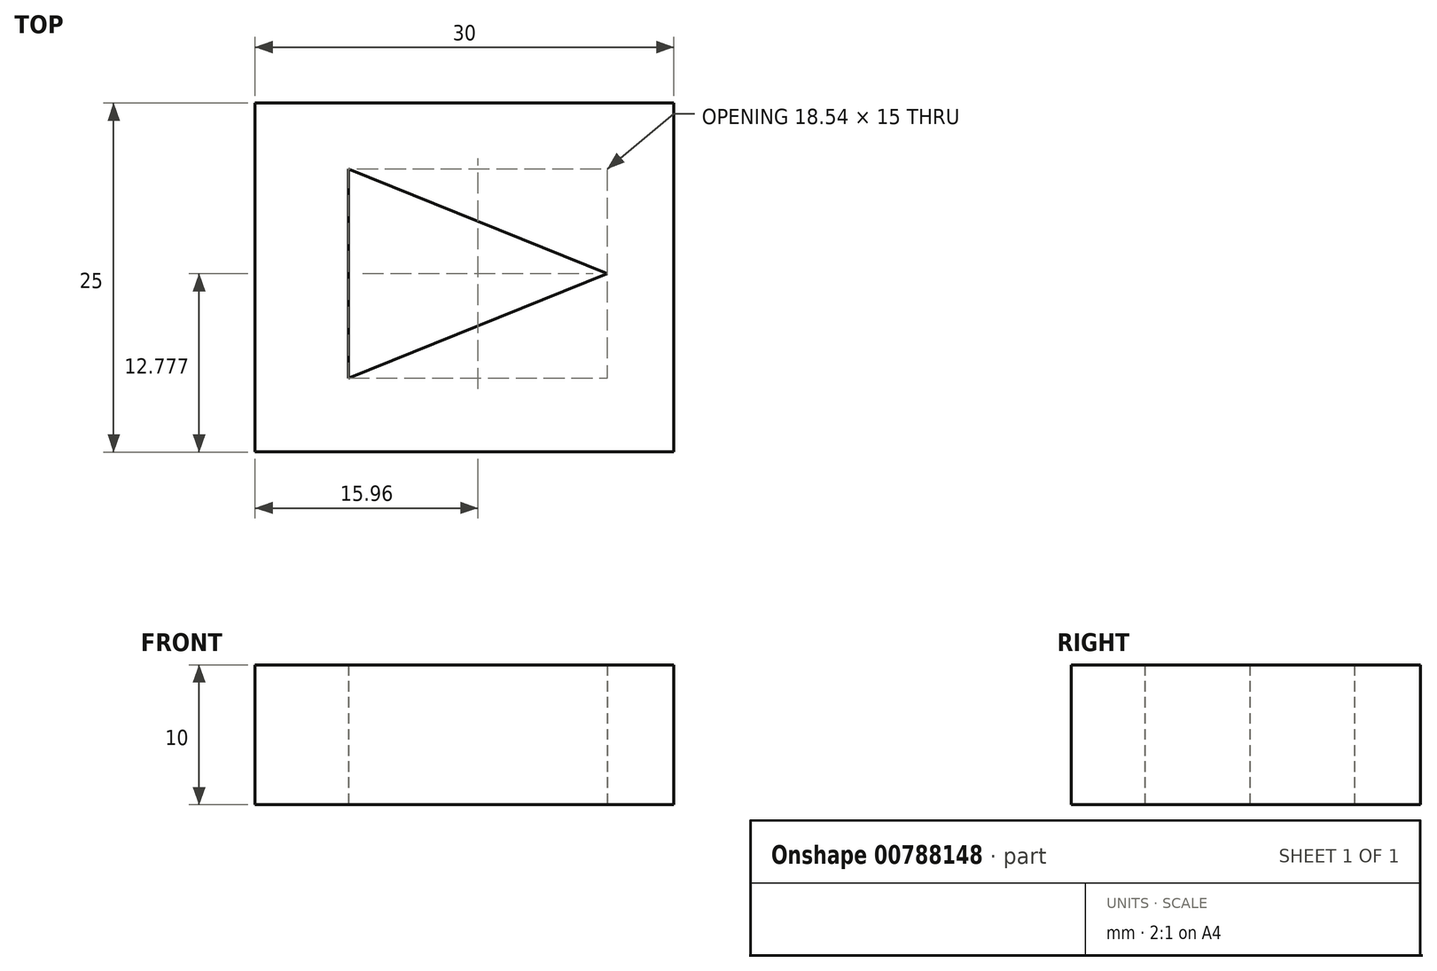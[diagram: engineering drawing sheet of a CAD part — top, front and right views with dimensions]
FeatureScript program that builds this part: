
annotation { "Feature Type Name" : "Feature", "Feature Type Description" : "" }
export const myFeature = defineFeature(function(context is Context, id is Id, definition is map)
    precondition{}
    {
        {
            var Q0;
            Q0=qCreatedBy(makeId("Top.planeOp"),FACE);
            var sketch = newSketch(context, id + "F0", { "sketchPlane" : qUnion([Q0])});
            skLineSegment(sketch, "E0.bottom", {"start": v(-26.14, 10.8) * mm, "end": v(3.86, 10.8) * mm});
            skLineSegment(sketch, "E0.top", {"start": v(-26.14, -14.2) * mm, "end": v(3.86, -14.2) * mm});
            skLineSegment(sketch, "E0.left", {"start": v(-26.14, 10.8) * mm, "end": v(-26.14, -14.2) * mm});
            skLineSegment(sketch, "E0.right", {"start": v(3.86, 10.8) * mm, "end": v(3.86, -14.2) * mm});
            skLineSegment(sketch, "E1", {"start": v(-19.45, 6.07) * mm, "end": v(-19.45, -8.93) * mm});
            skLineSegment(sketch, "E2", {"start": v(-19.45, -8.93) * mm, "end": v(-0.9, -1.43) * mm});
            skLineSegment(sketch, "E3", {"start": v(-0.9, -1.43) * mm, "end": v(-19.45, 6.07) * mm});
            skSolve(sketch);
        }
        {
            var Q0;
            Q0=makeQuery(id+"F0.imprint","IMPRINT",FACE,{"disambiguationData":[TD([[makeQuery(id+"F0.imprint","IMPRINT",EDGE,{"derivedFrom":sQuery(id+"F0.wireOp",EDGE,"E0.bottom")}),-1.0]])]});
            extrude(context, id + "F1", {"entities" : qUnion([Q0]), "depth" : 10 * mm, "offsetDistance" : 25 * mm});
        }
    });
